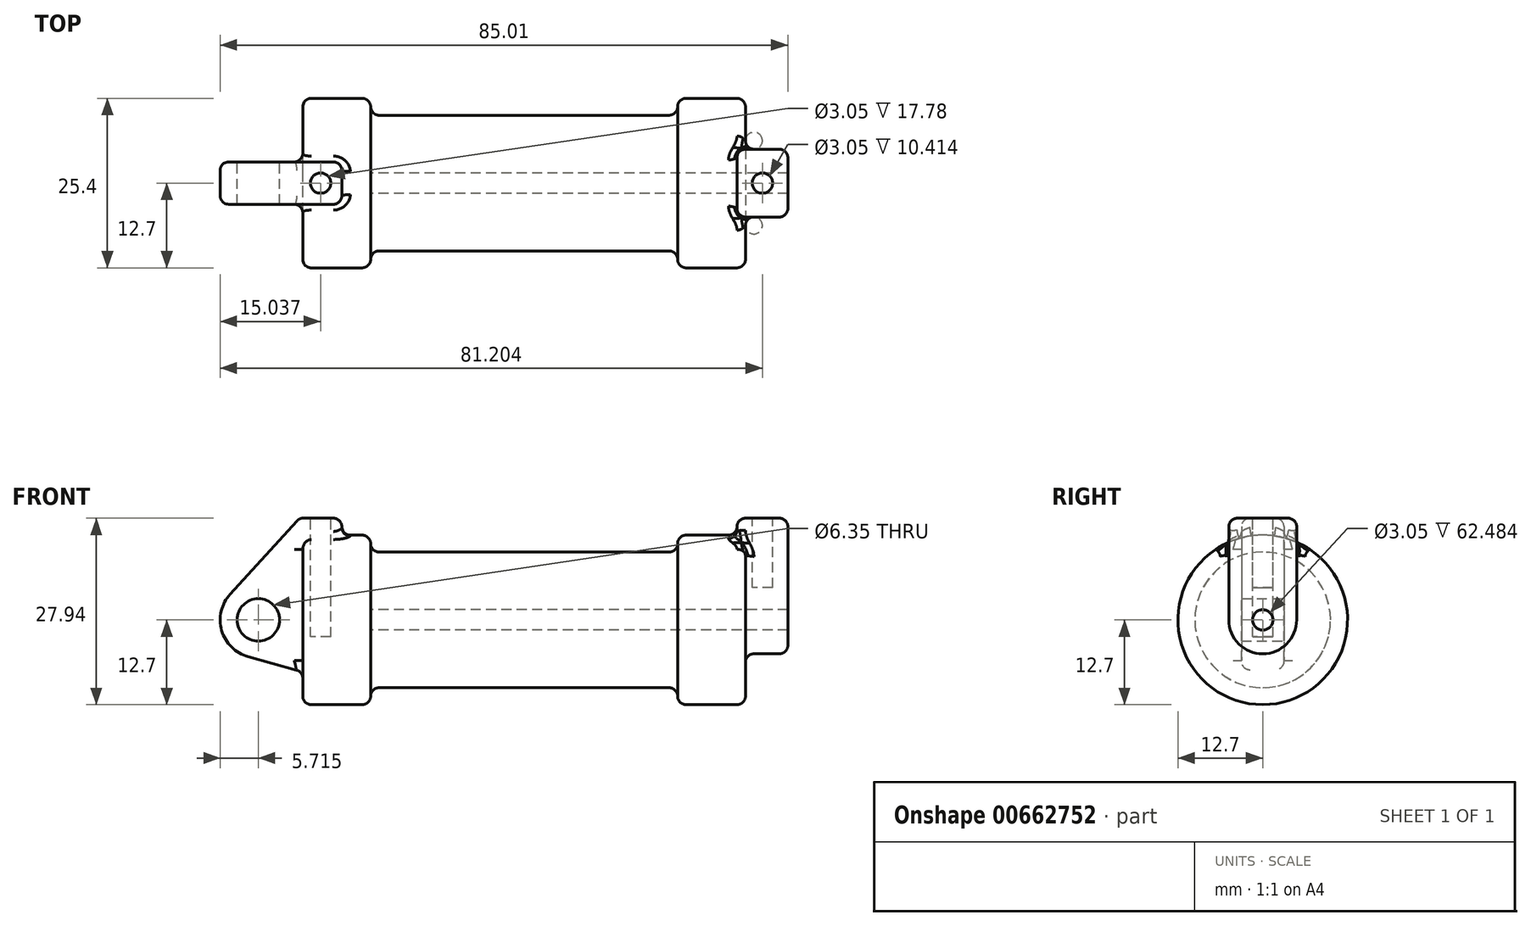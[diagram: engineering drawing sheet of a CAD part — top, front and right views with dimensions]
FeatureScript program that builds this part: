
annotation { "Feature Type Name" : "Feature", "Feature Type Description" : "" }
export const myFeature = defineFeature(function(context is Context, id is Id, definition is map)
    precondition{}
    {
        {
            var Q0;
            Q0=qCreatedBy(makeId("Front.planeOp"),FACE);
            var sketch = newSketch(context, id + "F0", { "sketchPlane" : qUnion([Q0])});
            skLineSegment(sketch, "E0", {"start": v(0, 0) * mm, "end": v(0, 12.7) * mm});
            skLineSegment(sketch, "E1", {"start": v(0, 12.7) * mm, "end": v(10.16, 12.7) * mm});
            skLineSegment(sketch, "E2", {"start": v(10.16, 12.7) * mm, "end": v(10.16, 10.16) * mm});
            skLineSegment(sketch, "E3", {"start": v(10.16, 10.16) * mm, "end": v(56.13, 10.16) * mm});
            skLineSegment(sketch, "E4", {"start": v(56.13, 10.16) * mm, "end": v(56.13, 12.7) * mm});
            skLineSegment(sketch, "E5", {"start": v(56.13, 12.7) * mm, "end": v(66.3, 12.7) * mm});
            skLineSegment(sketch, "E6", {"start": v(66.3, 12.7) * mm, "end": v(66.3, 0) * mm});
            skLineSegment(sketch, "E7", {"start": v(66.3, 0) * mm, "end": v(0, 0) * mm});
            skLineSegment(sketch, "E8", {"start": v(5.84, 15.24) * mm, "end": v(-0.5, 15.24) * mm});
            skLineSegment(sketch, "E9", {"start": v(-0.5, 15.24) * mm, "end": v(-10.88, 3.85) * mm});
            skLineSegment(sketch, "E10", {"start": v(0, 0) * mm, "end": v(-6.65, 0) * mm});
            skCircle(sketch, "E11", {"center": v(-6.65, 0) * mm, "radius": 5.72 * mm});
            skCircle(sketch, "E12", {"center": v(-6.65, 0) * mm, "radius": 3.18 * mm});
            skLineSegment(sketch, "E13", {"start": v(5.84, 15.24) * mm, "end": v(5.84, -9.4) * mm});
            skLineSegment(sketch, "E14", {"start": v(5.84, -9.4) * mm, "end": v(-8.18, -5.5) * mm});
            skSolve(sketch);
        }
        {
            var Q0;
            {var subQ0=sQuery(id+"F0.wireOp",EDGE,"E0");Q0=makeQuery(id+"F0.imprint","IMPRINT",FACE,{"disambiguationData":[TD([[makeQuery(id+"F0.imprint","IMPRINT",EDGE,{"derivedFrom":subQ0}),-1.0]])]});}
            var Q1;
            {var subQ0=sQuery(id+"F0.wireOp",EDGE,"E2");Q1=makeQuery(id+"F0.imprint","IMPRINT",FACE,{"disambiguationData":[TD([[makeQuery(id+"F0.imprint","IMPRINT",EDGE,{"derivedFrom":subQ0}),-1.0]])]});}
            var Q2;
            Q2=sQuery(id+"F0.wireOp",EDGE,"E7");
            revolve(context, id + "F1", {"entities" : qUnion([Q0, Q1]), "axis" : qUnion([Q2]), "revolveType" : RevolveType.FULL});
        }
        {
            var Q0;
            {var subQ1=sQuery(id+"F0.wireOp",EDGE,"E0");Q0=makeQuery(id+"F0.imprint","IMPRINT",FACE,{"disambiguationData":[TD([[makeQuery(id+"F0.imprint","IMPRINT",EDGE,{"derivedFrom":subQ1}),1.0]])]});}
            var Q1;
            {var subQ5=sQuery(id+"F0.wireOp",EDGE,"E12");Q1=makeQuery(id+"F0.imprint","IMPRINT",FACE,{"disambiguationData":[TD([[makeQuery(id+"F0.imprint","IMPRINT",EDGE,{"derivedFrom":subQ5}),-1.0]])]});}
            var Q2;
            {var subQ0=sQuery(id+"F0.wireOp",EDGE,"E14");Q2=makeQuery(id+"F0.imprint","IMPRINT",FACE,{"disambiguationData":[TD([[makeQuery(id+"F0.imprint","IMPRINT",EDGE,{"derivedFrom":subQ0}),-1.0]])]});}
            var Q3;
            {var subQ0=sQuery(id+"F0.wireOp",EDGE,"E0");Q3=makeQuery(id+"F0.imprint","IMPRINT",FACE,{"disambiguationData":[TD([[makeQuery(id+"F0.imprint","IMPRINT",EDGE,{"derivedFrom":subQ0}),-1.0]])]});}
            extrude(context, id + "F2", {"entities" : qUnion([Q0, Q1, Q2, Q3]), "operationType" : NewBodyOperationType.ADD, "endBound" : BoundingType.SYMMETRIC, "depth" : 6.35 * mm, "offsetDistance" : 25.4 * mm});
        }
        {
            var Q0;
            Q0=makeQuery(id+"F1.opRevolve","SWEPT_FACE",FACE,{"disambiguationData":[OSD([sQuery(id+"F0.wireOp",EDGE,"E6")])]});
            var sketch = newSketch(context, id + "F3", { "sketchPlane" : qUnion([Q0])});
            skCircle(sketch, "E15", {"center": v(0, 0) * mm, "radius": 1.52 * mm});
            skCircle(sketch, "E16", {"center": v(0, 0) * mm, "radius": 5.08 * mm});
            skLineSegment(sketch, "E17", {"start": v(5.08, 15.24) * mm, "end": v(5.08, 0) * mm});
            skLineSegment(sketch, "E18", {"start": v(-5.08, 15.24) * mm, "end": v(-5.08, 0) * mm});
            skLineSegment(sketch, "E19", {"start": v(-5.08, 15.24) * mm, "end": v(5.08, 15.24) * mm});
            skSolve(sketch);
        }
        {
            var Q0;
            Q0=makeQuery(id+"F3.imprint","IMPRINT",FACE,{"disambiguationData":[TD([[makeQuery(id+"F3.imprint","IMPRINT",EDGE,{"derivedFrom":sQuery(id+"F3.wireOp",EDGE,"E15")}),-1.0]])]});
            var Q1;
            {var subQ0=sQuery(id+"F3.wireOp",EDGE,"E17");var subQ1=sQuery(id+"F3.wireOp",EDGE,"E16");var subQ2=makeQuery(id+"F3.imprint","INTERSECT",VERTEX,{"derivedFrom":[subQ1,subQ0]});Q1=makeQuery(id+"F3.imprint","IMPRINT",FACE,{"disambiguationData":[TD([[makeQuery(id+"F3.imprint","IMPRINT",EDGE,{"disambiguationData":[TD([[subQ2,-1.0]])],"derivedFrom":subQ1}),-1.0]])]});}
            var Q2;
            {var subQ0=sQuery(id+"F3.wireOp",EDGE,"E19");Q2=makeQuery(id+"F3.imprint","IMPRINT",FACE,{"disambiguationData":[TD([[makeQuery(id+"F3.imprint","IMPRINT",EDGE,{"derivedFrom":subQ0}),-1.0]])]});}
            extrude(context, id + "F4", {"entities" : qUnion([Q0, Q1, Q2]), "operationType" : NewBodyOperationType.ADD, "depth" : 6.35 * mm, "offsetDistance" : 25.4 * mm, "hasSecondDirection" : true, "secondDirectionOppositeDirection" : true, "secondDirectionDepth" : 1.27 * mm});
        }
        {
            var Q0;
            Q0=makeQuery(id+"F4.boolean.opBoolean","SPLIT",FACE,{"disambiguationData":[TD([makeQuery(id+"F4.opExtrude","SWEPT_FACE",FACE,{"disambiguationData":[OSD([sQuery(id+"F3.wireOp",EDGE,"E15")])]})])],"derivedFrom":makeQuery(id+"F1.opRevolve","SWEPT_FACE",FACE,{"disambiguationData":[OSD([sQuery(id+"F0.wireOp",EDGE,"E6")])]})});
            var Q1;
            Q1=makeQuery(id+"F1.opRevolve","SWEPT_FACE",FACE,{"disambiguationData":[OSD([sQuery(id+"F0.wireOp",EDGE,"E2")])]});
            extrude(context, id + "F5", {"entities" : qUnion([Q0]), "operationType" : NewBodyOperationType.REMOVE, "endBound" : BoundingType.UP_TO_SURFACE, "oppositeDirection" : true, "depth" : 25.4 * mm, "endBoundEntityFace" : qUnion([Q1]), "offsetDistance" : 25.4 * mm});
        }
        {
            var Q0;
            Q0=makeQuery(id+"F2.opExtrude","SWEPT_FACE",FACE,{"disambiguationData":[OSD([sQuery(id+"F0.wireOp",EDGE,"E8")])]});
            var sketch = newSketch(context, id + "F6", { "sketchPlane" : qUnion([Q0])});
            skCircle(sketch, "E20", {"center": v(2.67, 0) * mm, "radius": 1.52 * mm});
            skPoint(sketch, "E20.centerSnap0", {"position": v(2.67, 3.18) * mm});
            skPoint(sketch, "E20.centerSnap1", {"position": v(-0.5, 0) * mm});
            skSolve(sketch);
        }
        {
            var Q0;
            Q0=makeQuery(id+"F4.opExtrude","SWEPT_FACE",FACE,{"disambiguationData":[OSD([sQuery(id+"F3.wireOp",EDGE,"E19")])]});
            var sketch = newSketch(context, id + "F7", { "sketchPlane" : qUnion([Q0])});
            skCircle(sketch, "E21", {"center": v(68.83, 0) * mm, "radius": 1.52 * mm});
            skPoint(sketch, "E21.centerSnap0", {"position": v(68.83, 5.08) * mm});
            skPoint(sketch, "E21.centerSnap1", {"position": v(65.02, 0) * mm});
            skSolve(sketch);
        }
        {
            var Q0;
            Q0=makeQuery(id+"F6.imprint","IMPRINT",FACE,{"disambiguationData":[TD([[makeQuery(id+"F6.imprint","IMPRINT",EDGE,{"derivedFrom":sQuery(id+"F6.wireOp",EDGE,"E20")}),1.0]])]});
            extrude(context, id + "F8", {"entities" : qUnion([Q0]), "operationType" : NewBodyOperationType.REMOVE, "oppositeDirection" : true, "depth" : 17.78 * mm, "offsetDistance" : 25.4 * mm});
        }
        {
            var Q0;
            Q0=makeQuery(id+"F7.imprint","IMPRINT",FACE,{"disambiguationData":[TD([[makeQuery(id+"F7.imprint","IMPRINT",EDGE,{"derivedFrom":sQuery(id+"F7.wireOp",EDGE,"E21")}),1.0]])]});
            extrude(context, id + "F9", {"entities" : qUnion([Q0]), "operationType" : NewBodyOperationType.REMOVE, "oppositeDirection" : true, "depth" : 10.4 * mm, "offsetDistance" : 25.4 * mm});
        }
        {
            var Q0;
            Q0=makeQuery(id+"F2.opExtrude","SWEPT_EDGE",EDGE,{"disambiguationData":[OSD([sQuery(id+"F0.wireOp",EDGE,"E8"),sQuery(id+"F0.wireOp",EDGE,"E9")])]});
            var Q1;
            Q1=makeQuery(id+"F2.opExtrude","CAP_EDGE",EDGE,{"disambiguationData":[OSD([sQuery(id+"F0.wireOp",EDGE,"E9")])],"isStart":true});
            var Q2;
            Q2=makeQuery(id+"F2.opExtrude","CAP_EDGE",EDGE,{"disambiguationData":[OSD([sQuery(id+"F0.wireOp",EDGE,"E9")])],"isStart":false});
            var Q3;
            Q3=makeQuery(id+"F1.opRevolve","SWEPT_EDGE",EDGE,{"disambiguationData":[OSD([sQuery(id+"F0.wireOp",EDGE,"E0"),sQuery(id+"F0.wireOp",EDGE,"E1")])]});
            var Q4;
            Q4=makeQuery(id+"F1.opRevolve","SWEPT_EDGE",EDGE,{"disambiguationData":[OSD([sQuery(id+"F0.wireOp",EDGE,"E1"),sQuery(id+"F0.wireOp",EDGE,"E2")])]});
            var Q5;
            Q5=makeQuery(id+"F2.opExtrude","CAP_EDGE",EDGE,{"disambiguationData":[OSD([sQuery(id+"F0.wireOp",EDGE,"E13")])],"isStart":false});
            var Q6;
            Q6=makeQuery(id+"F2.opExtrude","SWEPT_EDGE",EDGE,{"disambiguationData":[OSD([sQuery(id+"F0.wireOp",EDGE,"E8"),sQuery(id+"F0.wireOp",EDGE,"E13")])]});
            var Q7;
            Q7=makeQuery(id+"F2.opExtrude","CAP_EDGE",EDGE,{"disambiguationData":[OSD([sQuery(id+"F0.wireOp",EDGE,"E13")])],"isStart":true});
            var Q8;
            Q8=makeQuery(id+"F1.opRevolve","SWEPT_EDGE",EDGE,{"disambiguationData":[OSD([sQuery(id+"F0.wireOp",EDGE,"E4"),sQuery(id+"F0.wireOp",EDGE,"E5")])]});
            var Q9;
            Q9=makeQuery(id+"F1.opRevolve","SWEPT_EDGE",EDGE,{"disambiguationData":[OSD([sQuery(id+"F0.wireOp",EDGE,"E5"),sQuery(id+"F0.wireOp",EDGE,"E6")])]});
            var Q10;
            Q10=makeQuery(id+"F2.opExtrude","CAP_EDGE",EDGE,{"disambiguationData":[OSD([sQuery(id+"F0.wireOp",EDGE,"E8")])],"isStart":false});
            var Q11;
            Q11=makeQuery(id+"F2.opExtrude","CAP_EDGE",EDGE,{"disambiguationData":[OSD([sQuery(id+"F0.wireOp",EDGE,"E8")])],"isStart":true});
            var Q12;
            Q12=makeQuery(id+"F4.opExtrude","CAP_EDGE",EDGE,{"disambiguationData":[OSD([sQuery(id+"F3.wireOp",EDGE,"E16")])],"isStart":false});
            var Q13;
            Q13=makeQuery(id+"F4.boolean.opBoolean","INTERSECT",EDGE,{"derivedFrom":[makeQuery(id+"F1.opRevolve","SWEPT_FACE",FACE,{"disambiguationData":[OSD([sQuery(id+"F0.wireOp",EDGE,"E6")])]}),makeQuery(id+"F4.opExtrude","SWEPT_FACE",FACE,{"disambiguationData":[OSD([sQuery(id+"F3.wireOp",EDGE,"E18")])]})]});
            var Q14;
            Q14=makeQuery(id+"F4.boolean.opBoolean","INTERSECT",EDGE,{"derivedFrom":[makeQuery(id+"F1.opRevolve","SWEPT_FACE",FACE,{"disambiguationData":[OSD([sQuery(id+"F0.wireOp",EDGE,"E6")])]}),makeQuery(id+"F4.opExtrude","SWEPT_FACE",FACE,{"disambiguationData":[OSD([sQuery(id+"F3.wireOp",EDGE,"E16")])]})]});
            var Q15;
            Q15=makeQuery(id+"F4.opExtrude","CAP_EDGE",EDGE,{"disambiguationData":[OSD([sQuery(id+"F3.wireOp",EDGE,"E19")])],"isStart":false});
            var Q16;
            Q16=makeQuery(id+"F4.opExtrude","CAP_EDGE",EDGE,{"disambiguationData":[OSD([sQuery(id+"F3.wireOp",EDGE,"E19")])],"isStart":true});
            var Q17;
            Q17=makeQuery(id+"F4.opExtrude","SWEPT_EDGE",EDGE,{"disambiguationData":[OSD([sQuery(id+"F3.wireOp",EDGE,"E17"),sQuery(id+"F3.wireOp",EDGE,"E19")])]});
            var Q18;
            Q18=makeQuery(id+"F4.opExtrude","SWEPT_EDGE",EDGE,{"disambiguationData":[OSD([sQuery(id+"F3.wireOp",EDGE,"E18"),sQuery(id+"F3.wireOp",EDGE,"E19")])]});
            var Q19;
            Q19=makeQuery(id+"F2.boolean.opBoolean","INTERSECT",EDGE,{"derivedFrom":[makeQuery(id+"F1.opRevolve","SWEPT_FACE",FACE,{"disambiguationData":[OSD([sQuery(id+"F0.wireOp",EDGE,"E1")])]}),makeQuery(id+"F2.opExtrude","SWEPT_FACE",FACE,{"disambiguationData":[OSD([sQuery(id+"F0.wireOp",EDGE,"E13")])]})]});
            var Q20;
            Q20=makeQuery(id+"F4.opExtrude","CAP_EDGE",EDGE,{"disambiguationData":[OSD([sQuery(id+"F3.wireOp",EDGE,"E17")])],"isStart":false});
            var Q21;
            Q21=makeQuery(id+"F4.opExtrude","CAP_EDGE",EDGE,{"disambiguationData":[OSD([sQuery(id+"F3.wireOp",EDGE,"E18")])],"isStart":false});
            var Q22;
            Q22=makeQuery(id+"F4.boolean.opBoolean","INTERSECT",EDGE,{"derivedFrom":[makeQuery(id+"F1.opRevolve","SWEPT_FACE",FACE,{"disambiguationData":[OSD([sQuery(id+"F0.wireOp",EDGE,"E6")])]}),makeQuery(id+"F4.opExtrude","SWEPT_FACE",FACE,{"disambiguationData":[OSD([sQuery(id+"F3.wireOp",EDGE,"E17")])]})]});
            var Q23;
            Q23=makeQuery(id+"F4.opExtrude","CAP_EDGE",EDGE,{"disambiguationData":[OSD([sQuery(id+"F3.wireOp",EDGE,"E17")])],"isStart":true});
            var Q24;
            Q24=makeQuery(id+"F4.opExtrude","CAP_EDGE",EDGE,{"disambiguationData":[OSD([sQuery(id+"F3.wireOp",EDGE,"E18")])],"isStart":true});
            var Q25;
            Q25=makeQuery(id+"F2.opExtrude","CAP_EDGE",EDGE,{"disambiguationData":[OSD([sQuery(id+"F0.wireOp",EDGE,"E11")])],"isStart":false});
            var Q26;
            Q26=makeQuery(id+"F2.opExtrude","CAP_EDGE",EDGE,{"disambiguationData":[OSD([sQuery(id+"F0.wireOp",EDGE,"E14")])],"isStart":false});
            var Q27;
            Q27=makeQuery(id+"F2.opExtrude","CAP_EDGE",EDGE,{"disambiguationData":[OSD([sQuery(id+"F0.wireOp",EDGE,"E11")])],"isStart":true});
            var Q28;
            Q28=makeQuery(id+"F2.opExtrude","CAP_EDGE",EDGE,{"disambiguationData":[OSD([sQuery(id+"F0.wireOp",EDGE,"E14")])],"isStart":true});
            var Q29;
            Q29=makeQuery(id+"F2.boolean.opBoolean","INTERSECT",EDGE,{"derivedFrom":[makeQuery(id+"F1.opRevolve","SWEPT_FACE",FACE,{"disambiguationData":[OSD([sQuery(id+"F0.wireOp",EDGE,"E0")])]}),makeQuery(id+"F2.opExtrude","CAP_FACE",FACE,{"disambiguationData":[OSD([sQuery(id+"F0.wireOp",EDGE,"E8"),sQuery(id+"F0.wireOp",EDGE,"E9"),sQuery(id+"F0.wireOp",EDGE,"E11"),sQuery(id+"F0.wireOp",EDGE,"E12"),sQuery(id+"F0.wireOp",EDGE,"E13"),sQuery(id+"F0.wireOp",EDGE,"E14")])],"isStart":true})]});
            var Q30;
            Q30=makeQuery(id+"F2.boolean.opBoolean","INTERSECT",EDGE,{"derivedFrom":[makeQuery(id+"F1.opRevolve","SWEPT_FACE",FACE,{"disambiguationData":[OSD([sQuery(id+"F0.wireOp",EDGE,"E1")])]}),makeQuery(id+"F2.opExtrude","CAP_FACE",FACE,{"disambiguationData":[OSD([sQuery(id+"F0.wireOp",EDGE,"E8"),sQuery(id+"F0.wireOp",EDGE,"E9"),sQuery(id+"F0.wireOp",EDGE,"E11"),sQuery(id+"F0.wireOp",EDGE,"E12"),sQuery(id+"F0.wireOp",EDGE,"E13"),sQuery(id+"F0.wireOp",EDGE,"E14")])],"isStart":true})]});
            var Q31;
            Q31=makeQuery(id+"F2.boolean.opBoolean","INTERSECT",EDGE,{"derivedFrom":[makeQuery(id+"F1.opRevolve","SWEPT_FACE",FACE,{"disambiguationData":[OSD([sQuery(id+"F0.wireOp",EDGE,"E0")])]}),makeQuery(id+"F2.opExtrude","SWEPT_FACE",FACE,{"disambiguationData":[OSD([sQuery(id+"F0.wireOp",EDGE,"E14")])]})]});
            var Q32;
            Q32=makeQuery(id+"F4.boolean.opBoolean","INTERSECT",EDGE,{"derivedFrom":[makeQuery(id+"F1.opRevolve","SWEPT_FACE",FACE,{"disambiguationData":[OSD([sQuery(id+"F0.wireOp",EDGE,"E5")])]}),makeQuery(id+"F4.opExtrude","CAP_FACE",FACE,{"disambiguationData":[OSD([sQuery(id+"F3.wireOp",EDGE,"E15"),sQuery(id+"F3.wireOp",EDGE,"E16"),sQuery(id+"F3.wireOp",EDGE,"E17"),sQuery(id+"F3.wireOp",EDGE,"E18"),sQuery(id+"F3.wireOp",EDGE,"E19")])],"isStart":true})]});
            var Q33;
            Q33=makeQuery(id+"F2.boolean.opBoolean","INTERSECT",EDGE,{"derivedFrom":[makeQuery(id+"F1.opRevolve","SWEPT_FACE",FACE,{"disambiguationData":[OSD([sQuery(id+"F0.wireOp",EDGE,"E0")])]}),makeQuery(id+"F2.opExtrude","CAP_FACE",FACE,{"disambiguationData":[OSD([sQuery(id+"F0.wireOp",EDGE,"E8"),sQuery(id+"F0.wireOp",EDGE,"E9"),sQuery(id+"F0.wireOp",EDGE,"E11"),sQuery(id+"F0.wireOp",EDGE,"E12"),sQuery(id+"F0.wireOp",EDGE,"E13"),sQuery(id+"F0.wireOp",EDGE,"E14")])],"isStart":false})]});
            var Q34;
            Q34=makeQuery(id+"F1.opRevolve","SWEPT_FACE",FACE,{"disambiguationData":[OSD([sQuery(id+"F0.wireOp",EDGE,"E5")])]});
            var Q35;
            Q35=makeQuery(id+"F1.opRevolve","SWEPT_FACE",FACE,{"disambiguationData":[OSD([sQuery(id+"F0.wireOp",EDGE,"E1")])]});
            var Q36;
            Q36=makeQuery(id+"F4.opExtrude","SWEPT_FACE",FACE,{"disambiguationData":[OSD([sQuery(id+"F3.wireOp",EDGE,"E16")])]});
            fillet(context, id + "F10", {"entities" : qUnion([Q0, Q1, Q2, Q3, Q4, Q5, Q6, Q7, Q8, Q9, Q10, Q11, Q12, Q13, Q14, Q15, Q16, Q17, Q18, Q19, Q20, Q21, Q22, Q23, Q24, Q25, Q26, Q27, Q28, Q29, Q30, Q31, Q32, Q33, Q34, Q35, Q36]), "radius" : 1.27 * mm, "tangentPropagation" : true, "allowEdgeOverflow" : false});
        }
        {
            var Q0;
            Q0=makeQuery(id+"F1.opRevolve","SWEPT_EDGE",EDGE,{"disambiguationData":[OSD([sQuery(id+"F0.wireOp",EDGE,"E2"),sQuery(id+"F0.wireOp",EDGE,"E3")])]});
            fillet(context, id + "F11", {"entities" : qUnion([Q0]), "radius" : 1.27 * mm, "tangentPropagation" : true, "allowEdgeOverflow" : false});
        }
        {
            var Q0;
            Q0=makeQuery(id+"F1.opRevolve","SWEPT_EDGE",EDGE,{"disambiguationData":[OSD([sQuery(id+"F0.wireOp",EDGE,"E3"),sQuery(id+"F0.wireOp",EDGE,"E4")])]});
            fillet(context, id + "F12", {"entities" : qUnion([Q0]), "radius" : 1.27 * mm, "tangentPropagation" : true, "allowEdgeOverflow" : false});
        }
    });
